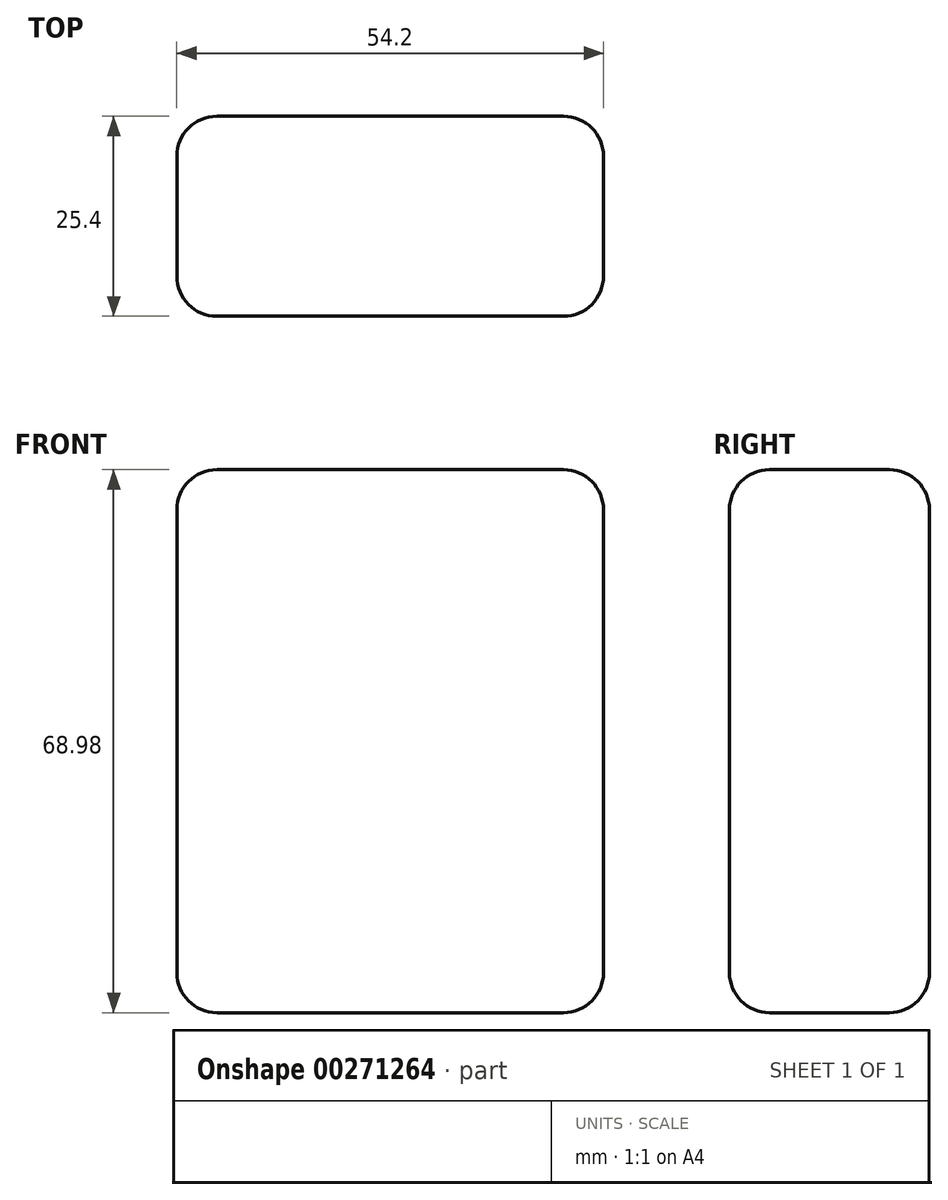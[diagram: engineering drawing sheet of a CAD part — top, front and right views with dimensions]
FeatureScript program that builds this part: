
annotation { "Feature Type Name" : "Feature", "Feature Type Description" : "" }
export const myFeature = defineFeature(function(context is Context, id is Id, definition is map)
    precondition{}
    {
        {
            var Q0;
            Q0=qCreatedBy(makeId("Front.planeOp"),FACE);
            var sketch = newSketch(context, id + "F0", { "sketchPlane" : qUnion([Q0])});
            skLineSegment(sketch, "E0.bottom", {"start": v(-31.73, 28.58) * mm, "end": v(22.47, 28.58) * mm});
            skLineSegment(sketch, "E0.top", {"start": v(-31.73, -40.4) * mm, "end": v(22.47, -40.4) * mm});
            skLineSegment(sketch, "E0.left", {"start": v(-31.73, 28.58) * mm, "end": v(-31.73, -40.4) * mm});
            skLineSegment(sketch, "E0.right", {"start": v(22.47, 28.58) * mm, "end": v(22.47, -40.4) * mm});
            skSolve(sketch);
        }
        {
            var Q0;
            Q0=makeQuery(id+"F0.imprint","IMPRINT",FACE,{"disambiguationData":[TD([[makeQuery(id+"F0.imprint","IMPRINT",EDGE,{"derivedFrom":sQuery(id+"F0.wireOp",EDGE,"E0.bottom")}),-1.0]])]});
            extrude(context, id + "F1", {"entities" : qUnion([Q0]), "depth" : 25.4 * mm});
        }
        {
            var Q0;
            Q0=makeQuery(id+"F1.opExtrude","SWEPT_EDGE",EDGE,{"disambiguationData":[OSD([sQuery(id+"F0.wireOp",EDGE,"E0.bottom"),sQuery(id+"F0.wireOp",EDGE,"E0.right")])]});
            var Q1;
            Q1=makeQuery(id+"F1.opExtrude","CAP_EDGE",EDGE,{"disambiguationData":[OSD([sQuery(id+"F0.wireOp",EDGE,"E0.right")])],"isStart":true});
            var Q2;
            Q2=makeQuery(id+"F1.opExtrude","CAP_EDGE",EDGE,{"disambiguationData":[OSD([sQuery(id+"F0.wireOp",EDGE,"E0.bottom")])],"isStart":false});
            fillet(context, id + "F2", {"entities" : qUnion([Q0, Q1, Q2]), "radius" : 5.08 * mm, "tangentPropagation" : true, "allowEdgeOverflow" : false});
        }
        {
            var Q0;
            Q0=makeQuery(id+"F1.opExtrude","CAP_EDGE",EDGE,{"disambiguationData":[OSD([sQuery(id+"F0.wireOp",EDGE,"E0.right")])],"isStart":false});
            var Q1;
            Q1=makeQuery(id+"F1.opExtrude","CAP_EDGE",EDGE,{"disambiguationData":[OSD([sQuery(id+"F0.wireOp",EDGE,"E0.bottom")])],"isStart":true});
            var Q2;
            Q2=makeQuery(id+"F1.opExtrude","SWEPT_EDGE",EDGE,{"disambiguationData":[OSD([sQuery(id+"F0.wireOp",EDGE,"E0.bottom"),sQuery(id+"F0.wireOp",EDGE,"E0.left")])]});
            var Q3;
            Q3=makeQuery(id+"F1.opExtrude","CAP_EDGE",EDGE,{"disambiguationData":[OSD([sQuery(id+"F0.wireOp",EDGE,"E0.left")])],"isStart":true});
            var Q4;
            Q4=makeQuery(id+"F1.opExtrude","CAP_EDGE",EDGE,{"disambiguationData":[OSD([sQuery(id+"F0.wireOp",EDGE,"E0.left")])],"isStart":false});
            var Q5;
            Q5=makeQuery(id+"F1.opExtrude","SWEPT_EDGE",EDGE,{"disambiguationData":[OSD([sQuery(id+"F0.wireOp",EDGE,"E0.top"),sQuery(id+"F0.wireOp",EDGE,"E0.right")])]});
            var Q6;
            Q6=makeQuery(id+"F1.opExtrude","CAP_EDGE",EDGE,{"disambiguationData":[OSD([sQuery(id+"F0.wireOp",EDGE,"E0.top")])],"isStart":false});
            var Q7;
            Q7=makeQuery(id+"F1.opExtrude","SWEPT_EDGE",EDGE,{"disambiguationData":[OSD([sQuery(id+"F0.wireOp",EDGE,"E0.top"),sQuery(id+"F0.wireOp",EDGE,"E0.left")])]});
            fillet(context, id + "F3", {"entities" : qUnion([Q0, Q1, Q2, Q3, Q4, Q5, Q6, Q7]), "radius" : 5.08 * mm, "tangentPropagation" : true, "allowEdgeOverflow" : false});
        }
    });
